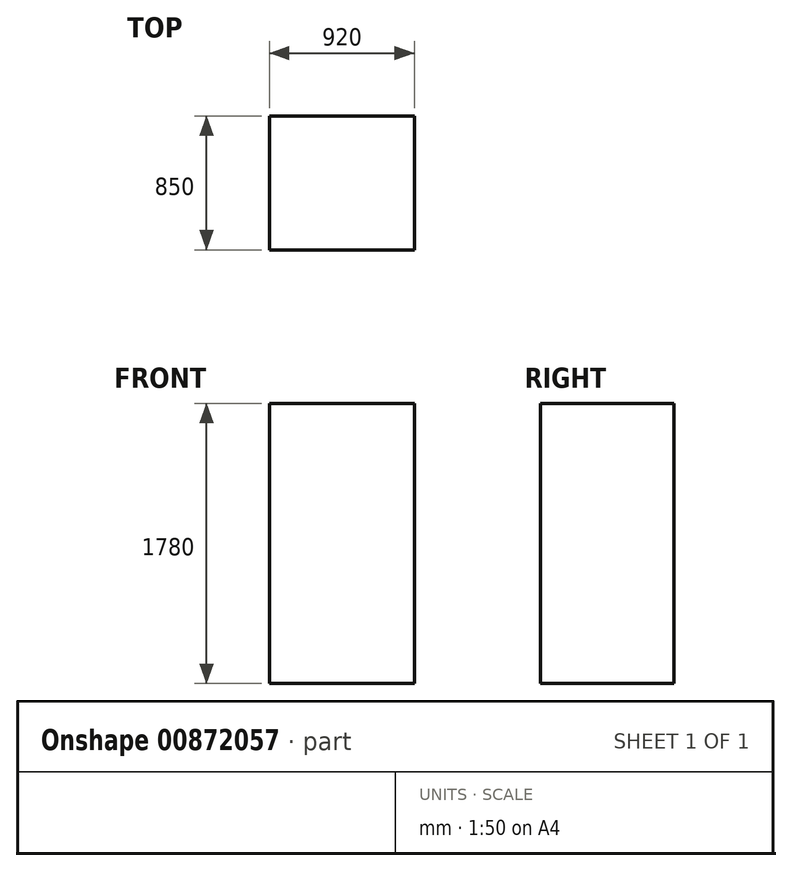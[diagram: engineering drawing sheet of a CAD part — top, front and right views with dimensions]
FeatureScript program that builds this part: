
annotation { "Feature Type Name" : "Feature", "Feature Type Description" : "" }
export const myFeature = defineFeature(function(context is Context, id is Id, definition is map)
    precondition{}
    {
        {
            var Q0;
            Q0=qCreatedBy(makeId("Top.planeOp"),FACE);
            var sketch = newSketch(context, id + "F0", { "sketchPlane" : qUnion([Q0])});
            skLineSegment(sketch, "E0.bottom", {"start": v(0, 0) * mm, "end": v(920, 0) * mm});
            skLineSegment(sketch, "E0.top", {"start": v(0, 850) * mm, "end": v(920, 850) * mm});
            skLineSegment(sketch, "E0.left", {"start": v(0, 0) * mm, "end": v(0, 850) * mm});
            skLineSegment(sketch, "E0.right", {"start": v(920, 0) * mm, "end": v(920, 850) * mm});
            skSolve(sketch);
        }
        {
            var Q0;
            Q0=qSketchRegion(id+"F0",true);
            extrude(context, id + "F1", {"entities" : qUnion([Q0]), "depth" : 1780 * mm, "offsetDistance" : 25 * mm});
        }
    });
